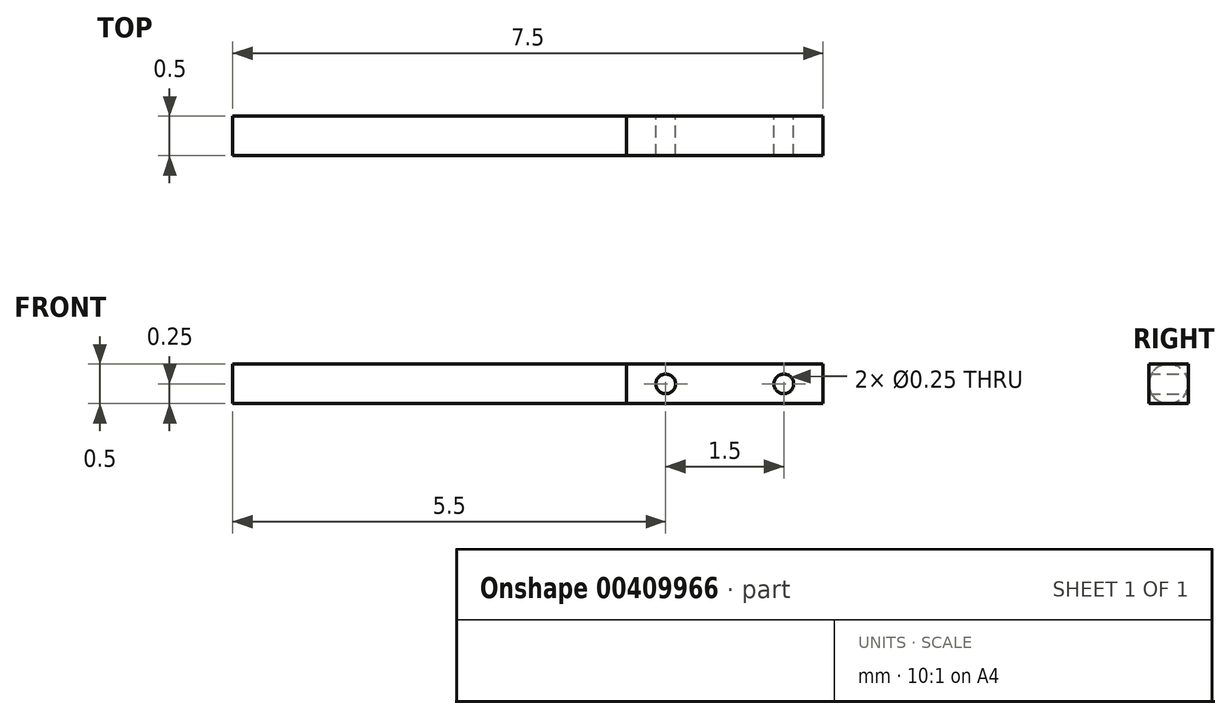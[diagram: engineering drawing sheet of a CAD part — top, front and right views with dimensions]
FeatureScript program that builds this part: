
annotation { "Feature Type Name" : "Feature", "Feature Type Description" : "" }
export const myFeature = defineFeature(function(context is Context, id is Id, definition is map)
    precondition{}
    {
        {
            var Q0;
            Q0=qCreatedBy(makeId("Right.planeOp"),FACE);
            var sketch = newSketch(context, id + "F0", { "sketchPlane" : qUnion([Q0])});
            skCircle(sketch, "E0", {"center": v(0, 0) * mm, "radius": 0.25 * mm});
            skSolve(sketch);
        }
        {
            var Q0;
            Q0=makeQuery(id+"F0.imprint","IMPRINT",FACE,{"disambiguationData":[TD([[makeQuery(id+"F0.imprint","IMPRINT",EDGE,{"derivedFrom":sQuery(id+"F0.wireOp",EDGE,"E0")}),1.0]])]});
            extrude(context, id + "F1", {"entities" : qUnion([Q0]), "depth" : 5 * mm});
        }
        {
            var Q0;
            Q0=makeQuery(id+"F1.opExtrude","CAP_FACE",FACE,{"disambiguationData":[OSD([sQuery(id+"F0.wireOp",EDGE,"E0")])],"isStart":false});
            var sketch = newSketch(context, id + "F2", { "sketchPlane" : qUnion([Q0])});
            skLineSegment(sketch, "E1.bottom", {"start": v(-0.25, 0.25) * mm, "end": v(0.25, 0.25) * mm});
            skLineSegment(sketch, "E1.top", {"start": v(-0.25, -0.25) * mm, "end": v(0.25, -0.25) * mm});
            skLineSegment(sketch, "E1.left", {"start": v(-0.25, 0.25) * mm, "end": v(-0.25, -0.25) * mm});
            skLineSegment(sketch, "E1.right", {"start": v(0.25, 0.25) * mm, "end": v(0.25, -0.25) * mm});
            skSolve(sketch);
        }
        {
            var Q0;
            {var subQ0=sQuery(id+"F2.wireOp",EDGE,"E1.right");var subQ1=sQuery(id+"F2.wireOp",EDGE,"E1.top");var subQ2=makeQuery(id+"F2.imprint","INTERSECT",VERTEX,{"derivedFrom":[subQ1,subQ0]});Q0=makeQuery(id+"F2.imprint","IMPRINT",FACE,{"disambiguationData":[TD([[makeQuery(id+"F2.imprint","IMPRINT",EDGE,{"disambiguationData":[TD([[subQ2,1.0]])],"derivedFrom":subQ1}),1.0]])]});}
            var Q1;
            {var subQ0=sQuery(id+"F2.wireOp",EDGE,"E1.right");var subQ1=sQuery(id+"F2.wireOp",EDGE,"E1.bottom");var subQ2=makeQuery(id+"F2.imprint","INTERSECT",VERTEX,{"derivedFrom":[subQ1,subQ0]});Q1=makeQuery(id+"F2.imprint","IMPRINT",FACE,{"disambiguationData":[TD([[makeQuery(id+"F2.imprint","IMPRINT",EDGE,{"disambiguationData":[TD([[subQ2,1.0]])],"derivedFrom":subQ1}),-1.0]])]});}
            var Q2;
            {var subQ0=makeQuery(id+"F1.opExtrude","CAP_EDGE",EDGE,{"disambiguationData":[OSD([sQuery(id+"F0.wireOp",EDGE,"E0")])],"isStart":false});var subQ1=makeQuery(id+"F2.imprint","INTERSECT",VERTEX,{"derivedFrom":[subQ0,sQuery(id+"F2.wireOp",EDGE,"E1.bottom")]});Q2=makeQuery(id+"F2.imprint","IMPRINT",FACE,{"disambiguationData":[TD([[makeQuery(id+"F2.imprint","IMPRINT",EDGE,{"disambiguationData":[TD([[subQ1,-1.0]])],"derivedFrom":subQ0}),1.0]])]});}
            var Q3;
            {var subQ0=sQuery(id+"F2.wireOp",EDGE,"E1.left");var subQ1=sQuery(id+"F2.wireOp",EDGE,"E1.bottom");var subQ2=makeQuery(id+"F2.imprint","INTERSECT",VERTEX,{"derivedFrom":[subQ1,subQ0]});Q3=makeQuery(id+"F2.imprint","IMPRINT",FACE,{"disambiguationData":[TD([[makeQuery(id+"F2.imprint","IMPRINT",EDGE,{"disambiguationData":[TD([[subQ2,-1.0]])],"derivedFrom":subQ1}),-1.0]])]});}
            var Q4;
            {var subQ0=sQuery(id+"F2.wireOp",EDGE,"E1.left");var subQ1=sQuery(id+"F2.wireOp",EDGE,"E1.top");var subQ2=makeQuery(id+"F2.imprint","INTERSECT",VERTEX,{"derivedFrom":[subQ1,subQ0]});Q4=makeQuery(id+"F2.imprint","IMPRINT",FACE,{"disambiguationData":[TD([[makeQuery(id+"F2.imprint","IMPRINT",EDGE,{"disambiguationData":[TD([[subQ2,-1.0]])],"derivedFrom":subQ1}),1.0]])]});}
            extrude(context, id + "F3", {"entities" : qUnion([Q0, Q1, Q2, Q3, Q4]), "operationType" : NewBodyOperationType.ADD, "depth" : 2.5 * mm});
        }
        {
            var Q0;
            Q0=makeQuery(id+"F3.opExtrude","SWEPT_FACE",FACE,{"disambiguationData":[OSD([sQuery(id+"F2.wireOp",EDGE,"E1.right")])]});
            var sketch = newSketch(context, id + "F4", { "sketchPlane" : qUnion([Q0])});
            skLineSegment(sketch, "E2", {"start": v(-8.34, 0) * mm, "end": v(-7.5, 0) * mm, "construction": true});
            skCircle(sketch, "E3", {"center": v(-7, 0) * mm, "radius": 0.12 * mm});
            skPoint(sketch, "E3.centerSnap0", {"position": v(-7.92, 0) * mm});
            skCircle(sketch, "E4", {"center": v(-5.5, 0) * mm, "radius": 0.12 * mm});
            skSolve(sketch);
        }
        {
            var Q0;
            Q0 = qSketchRegion(id + "F4", true);
            extrude(context, id + "F5", {"entities" : qUnion([Q0]), "operationType" : NewBodyOperationType.REMOVE, "oppositeDirection" : true, "depth" : 25 * mm});
        }
    });
